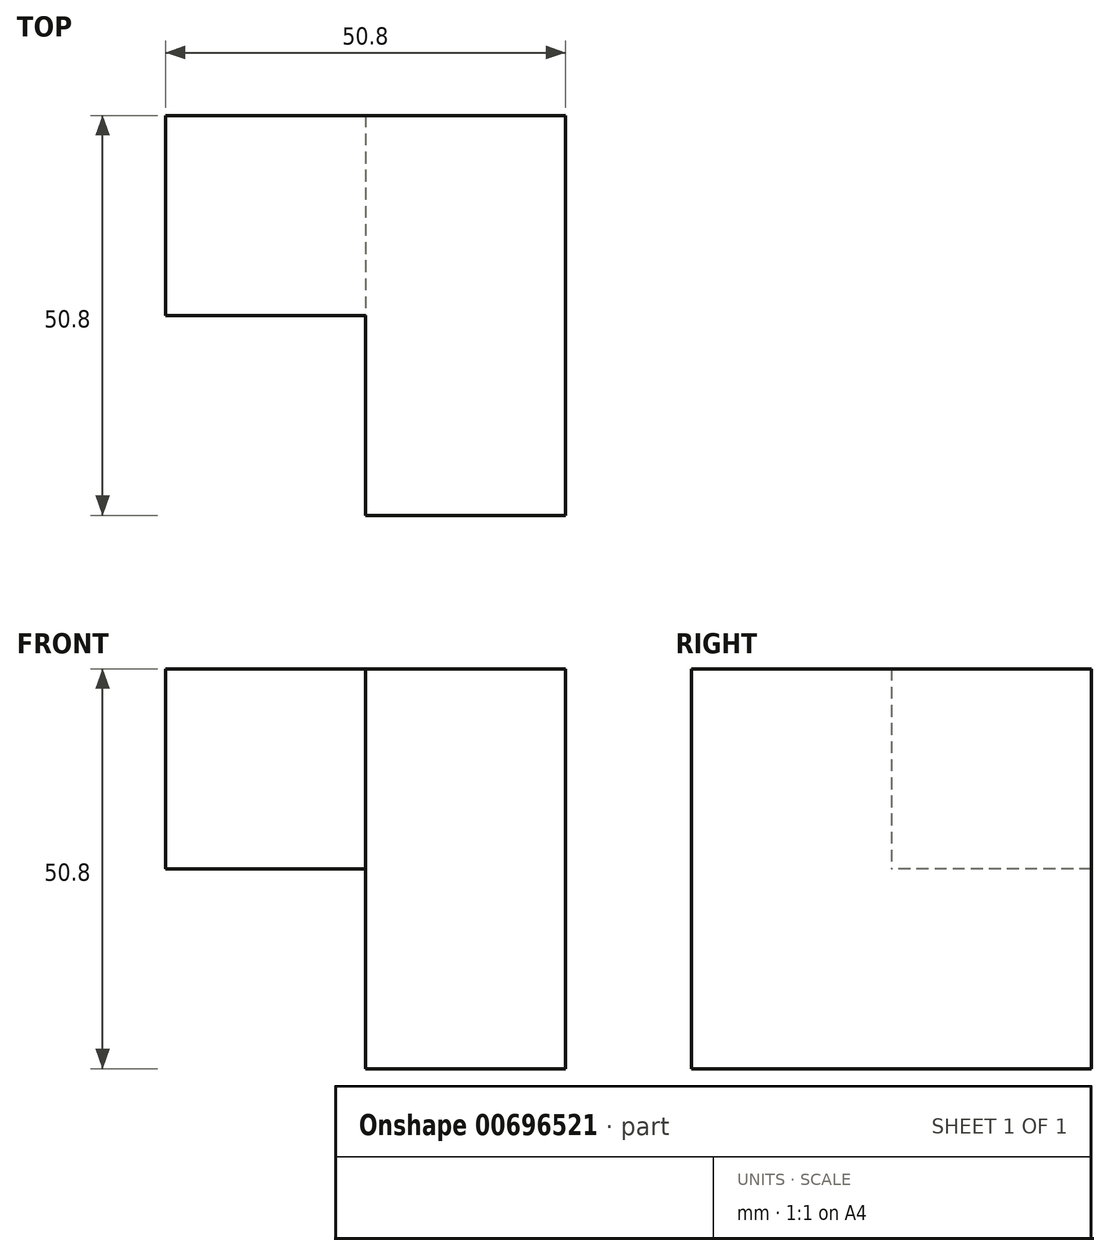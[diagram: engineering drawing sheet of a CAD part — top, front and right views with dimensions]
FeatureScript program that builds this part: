
annotation { "Feature Type Name" : "Feature", "Feature Type Description" : "" }
export const myFeature = defineFeature(function(context is Context, id is Id, definition is map)
    precondition{}
    {
        {
            var Q0;
            Q0=qCreatedBy(makeId("Front.planeOp"),FACE);
            var sketch = newSketch(context, id + "F0", { "sketchPlane" : qUnion([Q0])});
            skLineSegment(sketch, "E0", {"start": v(0, 0) * mm, "end": v(0, 50.8) * mm});
            skLineSegment(sketch, "E1", {"start": v(0, 50.8) * mm, "end": v(-25.4, 50.8) * mm});
            skLineSegment(sketch, "E2", {"start": v(-25.4, 50.8) * mm, "end": v(-25.4, 0) * mm});
            skLineSegment(sketch, "E3", {"start": v(-25.4, 0) * mm, "end": v(0, 0) * mm});
            skSolve(sketch);
        }
        {
            var Q0;
            Q0 = qSketchRegion(id + "F0", true);
            extrude(context, id + "F1", {"entities" : qUnion([Q0]), "depth" : 50.8 * mm, "offsetDistance" : 25.4 * mm});
        }
        {
            var Q0;
            Q0=makeQuery(id+"F1.opExtrude","SWEPT_FACE",FACE,{"disambiguationData":[OSD([sQuery(id+"F0.wireOp",EDGE,"E2")])]});
            var sketch = newSketch(context, id + "F2", { "sketchPlane" : qUnion([Q0])});
            skLineSegment(sketch, "E4.bottom", {"start": v(0, 50.8) * mm, "end": v(25.4, 50.8) * mm});
            skLineSegment(sketch, "E4.top", {"start": v(0, 25.4) * mm, "end": v(25.4, 25.4) * mm});
            skLineSegment(sketch, "E4.left", {"start": v(0, 50.8) * mm, "end": v(0, 25.4) * mm});
            skLineSegment(sketch, "E4.right", {"start": v(25.4, 50.8) * mm, "end": v(25.4, 25.4) * mm});
            skSolve(sketch);
        }
        {
            var Q0;
            Q0 = qSketchRegion(id + "F2", true);
            extrude(context, id + "F3", {"entities" : qUnion([Q0]), "operationType" : NewBodyOperationType.ADD, "depth" : 25.4 * mm, "offsetDistance" : 25.4 * mm});
        }
    });
